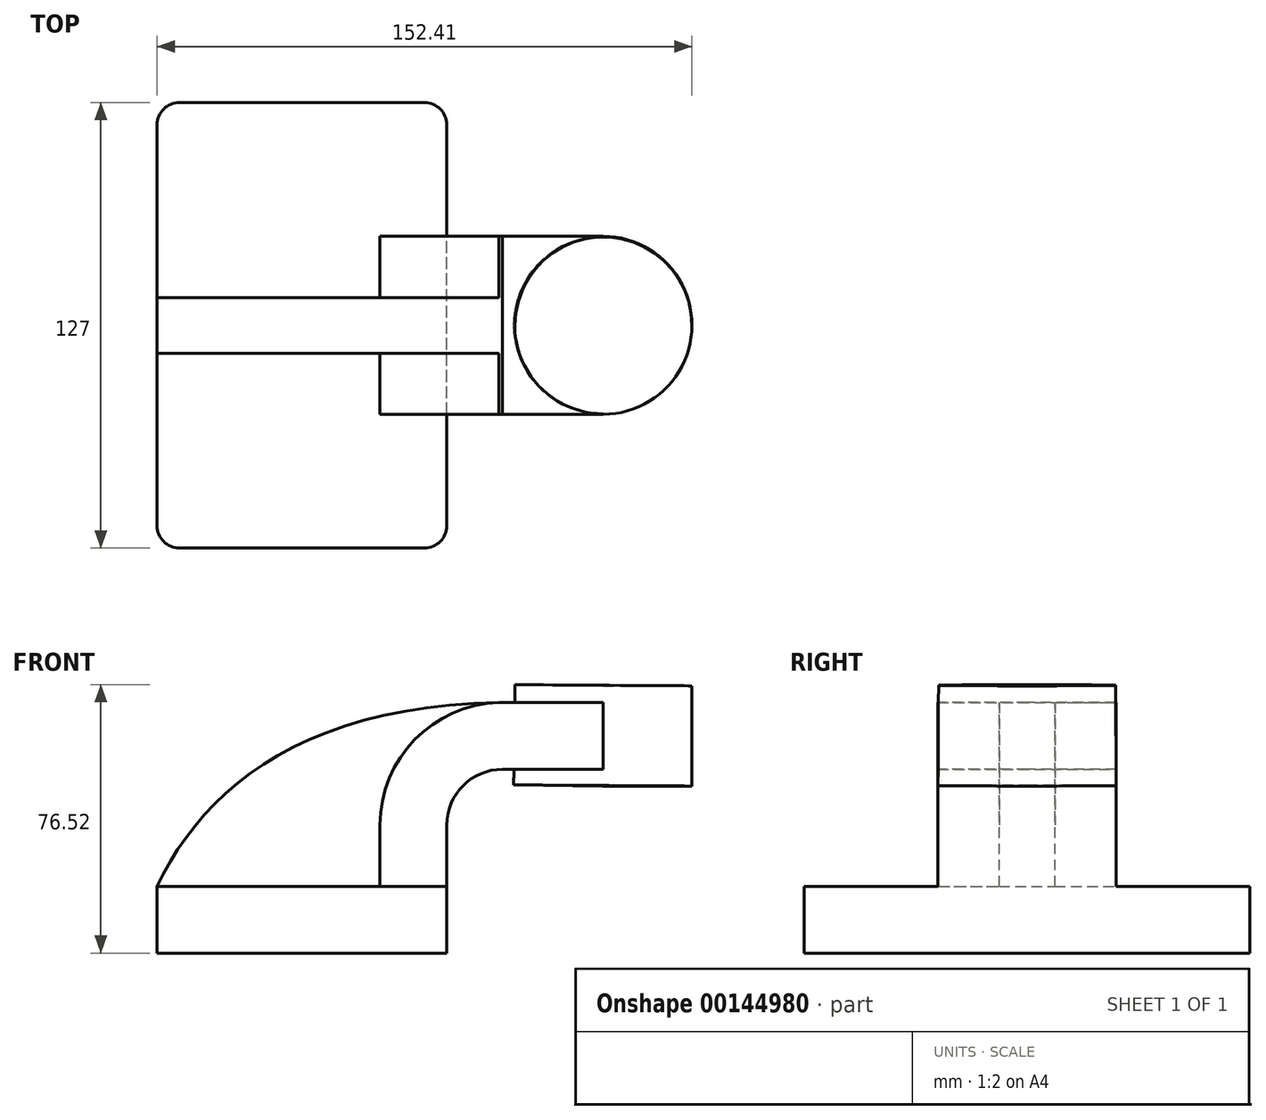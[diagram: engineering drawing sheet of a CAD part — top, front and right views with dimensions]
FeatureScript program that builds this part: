
annotation { "Feature Type Name" : "Feature", "Feature Type Description" : "" }
export const myFeature = defineFeature(function(context is Context, id is Id, definition is map)
    precondition{}
    {
        {
            var Q0;
            Q0=qCreatedBy(makeId("Front.planeOp"),FACE);
            var sketch = newSketch(context, id + "F0", { "sketchPlane" : qUnion([Q0])});
            skLineSegment(sketch, "E0.bottom", {"start": v(41.28, -9.53) * mm, "end": v(-41.28, -9.53) * mm});
            skLineSegment(sketch, "E0.top", {"start": v(41.28, 9.53) * mm, "end": v(-41.28, 9.52) * mm});
            skLineSegment(sketch, "E0.left", {"start": v(41.28, -9.53) * mm, "end": v(41.28, 9.53) * mm});
            skLineSegment(sketch, "E0.right", {"start": v(-41.28, -9.53) * mm, "end": v(-41.28, 9.52) * mm});
            skPoint(sketch, "E0.middle", {"position": v(0, 0) * mm});
            skLineSegment(sketch, "E1.bottom", {"start": v(111.12, 38.1) * mm, "end": v(60.32, 38.1) * mm});
            skLineSegment(sketch, "E1.top", {"start": v(111.12, 66.67) * mm, "end": v(60.32, 66.67) * mm});
            skLineSegment(sketch, "E1.left", {"start": v(111.12, 38.1) * mm, "end": v(111.12, 66.68) * mm});
            skLineSegment(sketch, "E1.right", {"start": v(60.32, 38.1) * mm, "end": v(60.32, 66.68) * mm});
            skPoint(sketch, "E1.middle", {"position": v(85.73, 52.39) * mm});
            skLineSegment(sketch, "E2", {"start": v(41.28, 9.53) * mm, "end": v(41.28, 27) * mm});
            skArc(sketch, "E3", {"start": v(41.28, 27) * mm, "mid": v(45.92, 38.23) * mm, "end": v(57.15, 42.88) * mm});
            skLineSegment(sketch, "E4", {"start": v(57.15, 42.88) * mm, "end": v(85.9, 42.88) * mm});
            skLineSegment(sketch, "E5.0", {"start": v(57.15, 61.93) * mm, "end": v(85.9, 61.93) * mm});
            skArc(sketch, "E5.1", {"start": v(22.23, 27) * mm, "mid": v(32.45, 51.7) * mm, "end": v(57.15, 61.93) * mm});
            skLineSegment(sketch, "E5.2", {"start": v(22.23, 9.53) * mm, "end": v(22.23, 27) * mm});
            skLineSegment(sketch, "E6", {"start": v(85.72, 38.1) * mm, "end": v(85.9, 66.67) * mm});
            skFitSpline(sketch, "E7", {"points": [v(-41.28, 9.52) * mm, v(57.15, 61.93) * mm], "startDerivative": vector(38.94, 82.26) * mm, "endDerivative": vector(171.45, 2.02) * mm});
            skSolve(sketch);
        }
        {
            var Q0;
            Q0=makeQuery(id+"F0.imprint","IMPRINT",FACE,{"disambiguationData":[TD([[makeQuery(id+"F0.imprint","IMPRINT",EDGE,{"derivedFrom":sQuery(id+"F0.wireOp",EDGE,"E0.bottom")}),-1.0]])]});
            extrude(context, id + "F1", {"entities" : qUnion([Q0]), "endBound" : BoundingType.SYMMETRIC, "depth" : 127 * mm});
        }
        {
            var Q0;
            {var subQ1=sQuery(id+"F0.wireOp",EDGE,"E2");Q0=makeQuery(id+"F0.imprint","IMPRINT",FACE,{"disambiguationData":[TD([[makeQuery(id+"F0.imprint","IMPRINT",EDGE,{"derivedFrom":subQ1}),1.0]])]});}
            var Q1;
            {var subQ0=sQuery(id+"F0.wireOp",EDGE,"E4");var subQ1=sQuery(id+"F0.wireOp",EDGE,"E1.right");var subQ2=makeQuery(id+"F0.imprint","INTERSECT",VERTEX,{"derivedFrom":[subQ1,subQ0]});Q1=makeQuery(id+"F0.imprint","IMPRINT",FACE,{"disambiguationData":[TD([[makeQuery(id+"F0.imprint","IMPRINT",EDGE,{"disambiguationData":[TD([[subQ2,-1.0]])],"derivedFrom":subQ1}),-1.0]])]});}
            extrude(context, id + "F2", {"entities" : qUnion([Q0, Q1]), "operationType" : NewBodyOperationType.ADD, "endBound" : BoundingType.SYMMETRIC, "depth" : 50.8 * mm});
        }
        {
            var Q0;
            {var subQ3=sQuery(id+"F0.wireOp",EDGE,"E5.2");Q0=makeQuery(id+"F0.imprint","IMPRINT",FACE,{"disambiguationData":[TD([[makeQuery(id+"F0.imprint","IMPRINT",EDGE,{"derivedFrom":subQ3}),1.0]])]});}
            extrude(context, id + "F3", {"entities" : qUnion([Q0]), "operationType" : NewBodyOperationType.ADD, "endBound" : BoundingType.SYMMETRIC, "depth" : 15.88 * mm});
        }
        {
            var Q0;
            {var subQ0=sQuery(id+"F0.wireOp",EDGE,"E1.left");Q0=makeQuery(id+"F0.imprint","IMPRINT",FACE,{"disambiguationData":[TD([[makeQuery(id+"F0.imprint","IMPRINT",EDGE,{"derivedFrom":subQ0}),1.0]])]});}
            var Q1;
            Q1=sQuery(id+"F0.wireOp",EDGE,"E6");
            revolve(context, id + "F4", {"operationType" : NewBodyOperationType.ADD, "entities" : qUnion([Q0]), "axis" : qUnion([Q1]), "revolveType" : RevolveType.FULL});
        }
        {
            var Q0;
            Q0=makeQuery(id+"F1.opExtrude","CAP_EDGE",EDGE,{"disambiguationData":[OSD([sQuery(id+"F0.wireOp",EDGE,"E0.left")])],"isStart":false});
            var Q1;
            Q1=makeQuery(id+"F1.opExtrude","CAP_EDGE",EDGE,{"disambiguationData":[OSD([sQuery(id+"F0.wireOp",EDGE,"E0.right")])],"isStart":false});
            var Q2;
            Q2=makeQuery(id+"F1.opExtrude","CAP_EDGE",EDGE,{"disambiguationData":[OSD([sQuery(id+"F0.wireOp",EDGE,"E0.left")])],"isStart":true});
            var Q3;
            Q3=makeQuery(id+"F1.opExtrude","CAP_EDGE",EDGE,{"disambiguationData":[OSD([sQuery(id+"F0.wireOp",EDGE,"E0.right")])],"isStart":true});
            fillet(context, id + "F5", {"entities" : qUnion([Q0, Q1, Q2, Q3]), "radius" : 6.35 * mm, "tangentPropagation" : true, "allowEdgeOverflow" : false});
        }
    });
